# Revit family: Overhead_Door-CHI_Overhead_Doors-MaxPro
name_source: partatom
category: Specialty Equipment
units: mm (PartAtom-declared; Revit-internal decimal feet)

## family parameters
Always vertical = Yes
Classification Number = 23.30.10.21
Cut with Voids When Loaded = No
Enable Cutting in Views = No
Host = Wall
Maintain Annotation Orientation = No
Part Type = Normal
Room Calculation Point = No
Round Connector Dimension = Use Diameter
Shared = No

## types (4) — shared parameters
Apparent Load Phase 1 = 0 VA
Apparent Load Phase 2 = 0 VA
Apparent Load Phase 3 = 0 VA
Assembly Code = B2030410
Closing Speed = Up to 12 inches / second
Curtain Material = Rubber - C.H.I Overhead Doors - Reinforced Black Rubber
Default Elevation = 0' - 0"
Description = Hight Performance Rubber Door
Door Rail Depth = 0' - 6"
Keynote = 08 30 00
Load Classification = Motor
Manufacturer = C.H.I. Overhead Doors
Manufacturer Fax Number = 800-677-2650
Material = Metal - C.H.I Overhead Doors - Safety Yellow
Motor Distance from Wall = 2' - 0"
Motor Side Offset = 1' - 2"
Number of Poles = 3
Opening Speed = Up to 12 inches / second
Panel Thickness = 0' - 0 1/4"
Power Factor = 1
Product Documentation Link = https://www.chiohd.com
Product Page URL = https://www.chiohd.com
Steel Gauge = 1/4"
URL = https://www.chiohd.com
Version = 2021-v1.a
Voltage = 0 V
Warranty URL = https://www.chiohd.com

## per-type parameters (varying)
| type | Axis Offset | Axis to Wall | C Model | Door Rail Width | Model | Motor Distance to Shutterbox | Motor Length | Shutter Box Depth | Shutter Box Height |
| MaxPro - 350 - Safety Yellow - 1/4" Reinforced Rubber | 1' - 0" | 0' - 7 1/2" | 1 | 0' - 5" | 350 | 0' - 8 5/8" | 1' - 4 1/2" | 1' - 3" | 1' - 3" |
| MaxPro - 350 Standard Guides - Safety Yellow - 1/4" Reinforced Rubber | 1' - 0" | 0' - 9" | 2 | 0' - 3 1/2" | 350 Standard Guides | 0' - 10 1/8" | 1' - 4 1/2" | 1' - 3" | 1' - 3" |
| MaxPro - 800 - Safety Yellow - 1/4" Reinforced Rubber Curtain | 0' - 10" | 0' - 9" | 3 | 0' - 5" | 800 | 0' - 8 5/8" | 1' - 3" | 1' - 6" | 1' - 6" |
| MaxPro - 800 Standard Guides - Safety Yellow - 1/4" Reinforced Rubber | 0' - 10" | 0' - 9" | 4 | 0' - 3 1/2" | 800 Standard Guides | 0' - 10 1/8" | 1' - 3" | 1' - 6" | 1' - 6" |

## geometry (parser evidence)
native form markers: Extrusion x1, Sweep x12
no freeform markers — native parametric forms only
